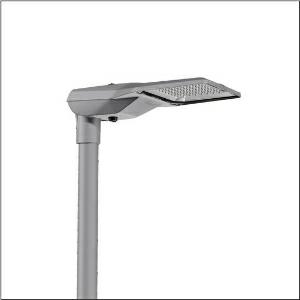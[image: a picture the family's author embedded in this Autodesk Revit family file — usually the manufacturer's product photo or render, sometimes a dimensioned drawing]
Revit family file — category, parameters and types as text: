
# Revit family: streetlight_sl_21_midi___pc-l_5xe3f33t08mb_a9f3
name_source: partatom
category: Lighting Fixtures
units: mm (PartAtom-declared; Revit-internal decimal feet)

## family parameters
Cut with Voids When Loaded = No
Host = Face
Light Source = No
Part Type = Normal
Room Calculation Point = No
Round Connector Dimension = Use Diameter
Shared = No

## types (1)
- --- (1 x LED, 17390 lm, 136 W, 3000K)
    Apparent Load = 136 VA
    CIE Flux Codes = 38 78 98 100 100
    Color Rendering = 70
    Color Temperature = 3000K
    Default Elevation = 1800 mm
    Description = Streetlight SL 21 midi, mast luminaire, primary light control with lens, of PMMA, primary optical cover: cover, of toughened safety glass, transparent, light distribution: PC-L, light emission: direct distribution, primary light characteristic: asymmetric, left, installation type: side-entry, post-top, LED, High Power LED, rated luminous flux: 17.390lm, luminous efficacy: 128lm/W, light colour: 730, colour temperature: 3000K, control gear: D4i, control: overheat protection, constant luminous flux control, time-dependent luminous flux control, flexible luminous flux parameterisation, pre-setting: logarithmic dimming characteristic, mains connection: 230..240V, AC, 50/60Hz, start of lifetime: 136W, end of service life: 142W, reduction: 61W, luminaire housing, of diecast aluminium, powder-coated, Siteco® metallic grey (DB 702S), corrosivity category C5 mid according to DIN EN ISO 12944, please order mast flange separately, inclination adjustable: 0°, 5°, 10°, 15°, sealing non-destructively replaceable, multi-level sealing system, length: 644mm, width: 335mm, height: 110mm, mast flange for spigot size: 42mm (side-entry): 5XC10008XM4, 60/48mm (side-entry/post-top): 5XC10108XM2, 76/60mm (side-entry/post-top): 5XC10108XM1, mounting height: 4..8m, Smart Interface below and above, protection rating (complete): IP66, insulation class (complete): insulation class II (safety insulation), certification: CE, ENEC, ENEC+, VDE, impact resistance: IK10, permissible operating ambient temperature for outdoor applications: -40..+50°C, standard-compliant lighting for roads and squares, packaging unit: 1 piece

Light Distribution: PC-L
    Height = 111 mm
    Lamp = 1 x LED
    Lamp Light Flux = 17390 lm
    Lamp Power = 136 W
    Lamp count = 1
    Length = 644 mm
    Luminous efficacy = 128 lm/W
    Manufacturer = Siteco
    ModVariant = No
    Model = 5XE3F33T08MB
    Number of Poles = 1
    OnlyDefault = Yes
    Power Factor = 1
    Product Name = Streetlight SL 21 midi | PC-L
    Product group = mast luminaire | pylon top
    ProductGroupID = 6100
    Protection Class = Protection class II
    Protection Degree = IP 66
    RLX_Detail_Level = 1
    RLX_Emergency_Light_Flux = 0 lm
    RLX_Emergency_Type = 0
    RLX_Emergency_Type_DB = No
    RlxData = <blob elided: 29621 chars, md5=066b6d6c>
    Socket = socket
    Standby Power = 0 W
    System Light Flux = 17390 lm
    System Power = 136 W
    Type Comments = factory setting: luminous flux: 100 % | dim-lin: 254 | 695 mA
    Type Image = l_1004304.jpg
    URL = http://relux.com
    VarID = @adj_064692
    Voltage = 0 V
    Weight = 0.00 kg
    Width = 336 mm

## geometry (parser evidence)
native form markers: Blend x4, Sweep x10
no freeform markers — native parametric forms only
